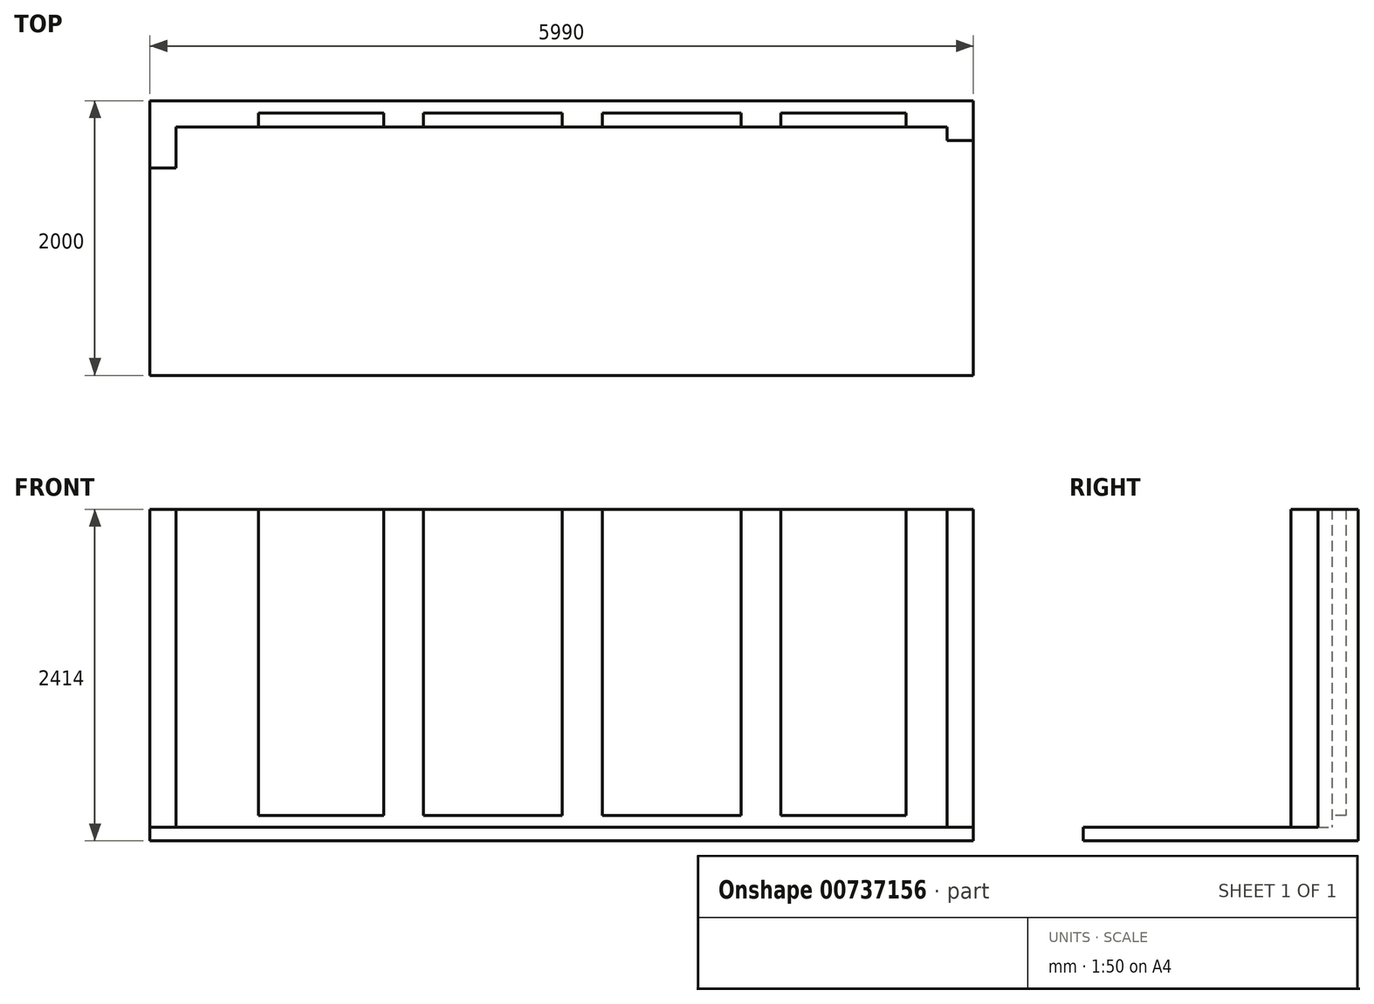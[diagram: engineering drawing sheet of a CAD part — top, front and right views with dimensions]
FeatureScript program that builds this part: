
annotation { "Feature Type Name" : "Feature", "Feature Type Description" : "" }
export const myFeature = defineFeature(function(context is Context, id is Id, definition is map)
    precondition{}
    {
        {
            var Q0;
            Q0=qCreatedBy(makeId("Top.planeOp"),FACE);
            var sketch = newSketch(context, id + "F0", { "sketchPlane" : qUnion([Q0])});
            skLineSegment(sketch, "E0.top", {"start": v(2995, 0) * mm, "end": v(-2995, 0) * mm});
            skLineSegment(sketch, "E0.right", {"start": v(-2995, -490) * mm, "end": v(-2995, 0) * mm});
            skPoint(sketch, "E0.middle", {"position": v(0, 0) * mm});
            skLineSegment(sketch, "E1", {"start": v(-2995, -490) * mm, "end": v(-2805, -490) * mm});
            skLineSegment(sketch, "E2", {"start": v(-2805, -490) * mm, "end": v(-2805, -190) * mm});
            skLineSegment(sketch, "E3", {"start": v(-2805, -190) * mm, "end": v(-2205, -190) * mm});
            skLineSegment(sketch, "E4", {"start": v(-2205, -90) * mm, "end": v(-2205, -190) * mm});
            skLineSegment(sketch, "E5", {"start": v(-2205, -90) * mm, "end": v(-1295, -90) * mm});
            skLineSegment(sketch, "E6", {"start": v(-1295, -190) * mm, "end": v(-1295, -90) * mm});
            skLineSegment(sketch, "E7", {"start": v(-1295, -190) * mm, "end": v(-1005, -190) * mm});
            skLineSegment(sketch, "E8", {"start": v(-1005, -90) * mm, "end": v(-1005, -190) * mm});
            skLineSegment(sketch, "E9", {"start": v(-1005, -90) * mm, "end": v(5, -90) * mm});
            skLineSegment(sketch, "E10", {"start": v(5, -190) * mm, "end": v(5, -90) * mm});
            skLineSegment(sketch, "E11", {"start": v(5, -190) * mm, "end": v(295, -190) * mm});
            skLineSegment(sketch, "E12", {"start": v(295, -190) * mm, "end": v(295, -90) * mm});
            skLineSegment(sketch, "E13", {"start": v(295, -90) * mm, "end": v(1305, -90) * mm});
            skLineSegment(sketch, "E14", {"start": v(1305, -90) * mm, "end": v(1305, -190) * mm});
            skLineSegment(sketch, "E15", {"start": v(1305, -190) * mm, "end": v(1595, -190) * mm});
            skLineSegment(sketch, "E16", {"start": v(1595, -190) * mm, "end": v(1595, -90) * mm});
            skLineSegment(sketch, "E17", {"start": v(1595, -90) * mm, "end": v(2505, -90) * mm});
            skLineSegment(sketch, "E18", {"start": v(2505, -90) * mm, "end": v(2505, -190) * mm});
            skLineSegment(sketch, "E19", {"start": v(2505, -190) * mm, "end": v(2805, -190) * mm});
            skLineSegment(sketch, "E20", {"start": v(2805, -190) * mm, "end": v(2805, -290) * mm});
            skLineSegment(sketch, "E21", {"start": v(2805, -290) * mm, "end": v(2995, -290) * mm});
            skLineSegment(sketch, "E22", {"start": v(2995, 0) * mm, "end": v(2995, -290) * mm});
            skSolve(sketch);
        }
        {
            var Q0;
            Q0 = qSketchRegion(id + "F0", true);
            extrude(context, id + "F1", {"entities" : qUnion([Q0]), "depth" : 2314 * mm, "offsetDistance" : 25 * mm});
        }
        {
            var Q0;
            Q0=makeQuery(id+"F1.opExtrude","CAP_FACE",FACE,{"disambiguationData":[OSD([sQuery(id+"F0.wireOp",EDGE,"E0.top"),sQuery(id+"F0.wireOp",EDGE,"E0.right"),sQuery(id+"F0.wireOp",EDGE,"E1"),sQuery(id+"F0.wireOp",EDGE,"E2"),sQuery(id+"F0.wireOp",EDGE,"E3"),sQuery(id+"F0.wireOp",EDGE,"E4"),sQuery(id+"F0.wireOp",EDGE,"E5"),sQuery(id+"F0.wireOp",EDGE,"E6"),sQuery(id+"F0.wireOp",EDGE,"E7"),sQuery(id+"F0.wireOp",EDGE,"E8"),sQuery(id+"F0.wireOp",EDGE,"E9"),sQuery(id+"F0.wireOp",EDGE,"E10"),sQuery(id+"F0.wireOp",EDGE,"E11"),sQuery(id+"F0.wireOp",EDGE,"E12"),sQuery(id+"F0.wireOp",EDGE,"E13"),sQuery(id+"F0.wireOp",EDGE,"E14"),sQuery(id+"F0.wireOp",EDGE,"E15"),sQuery(id+"F0.wireOp",EDGE,"E16"),sQuery(id+"F0.wireOp",EDGE,"E17"),sQuery(id+"F0.wireOp",EDGE,"E18"),sQuery(id+"F0.wireOp",EDGE,"E19"),sQuery(id+"F0.wireOp",EDGE,"E20"),sQuery(id+"F0.wireOp",EDGE,"E21"),sQuery(id+"F0.wireOp",EDGE,"E22")])],"isStart":true});
            var sketch = newSketch(context, id + "F2", { "sketchPlane" : qUnion([Q0])});
            skLineSegment(sketch, "E23.bottom", {"start": v(-2995, 0) * mm, "end": v(2995, 0) * mm});
            skLineSegment(sketch, "E23.top", {"start": v(-2995, 2000) * mm, "end": v(2995, 2000) * mm});
            skLineSegment(sketch, "E23.left", {"start": v(-2995, 0) * mm, "end": v(-2995, 2000) * mm});
            skLineSegment(sketch, "E23.right", {"start": v(2995, 0) * mm, "end": v(2995, 2000) * mm});
            skSolve(sketch);
        }
        {
            var Q0;
            Q0 = qSketchRegion(id + "F2", true);
            extrude(context, id + "F3", {"entities" : qUnion([Q0]), "operationType" : NewBodyOperationType.ADD, "depth" : 100 * mm, "offsetDistance" : 25 * mm});
        }
        {
            var Q0;
            Q0=makeQuery(id+"F3.opExtrude","CAP_FACE",FACE,{"disambiguationData":[OSD([sQuery(id+"F2.wireOp",EDGE,"E23.bottom"),sQuery(id+"F2.wireOp",EDGE,"E23.top"),sQuery(id+"F2.wireOp",EDGE,"E23.left"),sQuery(id+"F2.wireOp",EDGE,"E23.right")])],"isStart":true});
            var sketch = newSketch(context, id + "F4", { "sketchPlane" : qUnion([Q0])});
            skLineSegment(sketch, "E24.bottom", {"start": v(-2205, -90) * mm, "end": v(-1295, -90) * mm});
            skLineSegment(sketch, "E24.top", {"start": v(-2205, -190) * mm, "end": v(-1295, -190) * mm});
            skLineSegment(sketch, "E24.left", {"start": v(-2205, -90) * mm, "end": v(-2205, -190) * mm});
            skLineSegment(sketch, "E24.right", {"start": v(-1295, -90) * mm, "end": v(-1295, -190) * mm});
            skLineSegment(sketch, "E25.bottom", {"start": v(-1005, -90) * mm, "end": v(5, -90) * mm});
            skLineSegment(sketch, "E25.top", {"start": v(-1005, -190) * mm, "end": v(5, -190) * mm});
            skLineSegment(sketch, "E25.left", {"start": v(-1005, -90) * mm, "end": v(-1005, -190) * mm});
            skLineSegment(sketch, "E25.right", {"start": v(5, -90) * mm, "end": v(5, -190) * mm});
            skLineSegment(sketch, "E26.bottom", {"start": v(295, -90) * mm, "end": v(1305, -90) * mm});
            skLineSegment(sketch, "E26.top", {"start": v(295, -190) * mm, "end": v(1305, -190) * mm});
            skLineSegment(sketch, "E26.left", {"start": v(295, -90) * mm, "end": v(295, -190) * mm});
            skLineSegment(sketch, "E26.right", {"start": v(1305, -90) * mm, "end": v(1305, -190) * mm});
            skLineSegment(sketch, "E27.bottom", {"start": v(1595, -90) * mm, "end": v(2505, -90) * mm});
            skLineSegment(sketch, "E27.top", {"start": v(1595, -190) * mm, "end": v(2505, -190) * mm});
            skLineSegment(sketch, "E27.left", {"start": v(1595, -90) * mm, "end": v(1595, -190) * mm});
            skLineSegment(sketch, "E27.right", {"start": v(2505, -90) * mm, "end": v(2505, -190) * mm});
            skSolve(sketch);
        }
        {
            var Q0;
            Q0 = qSketchRegion(id + "F4", true);
            extrude(context, id + "F5", {"entities" : qUnion([Q0]), "operationType" : NewBodyOperationType.ADD, "depth" : 86 * mm, "offsetDistance" : 25 * mm});
        }
    });
